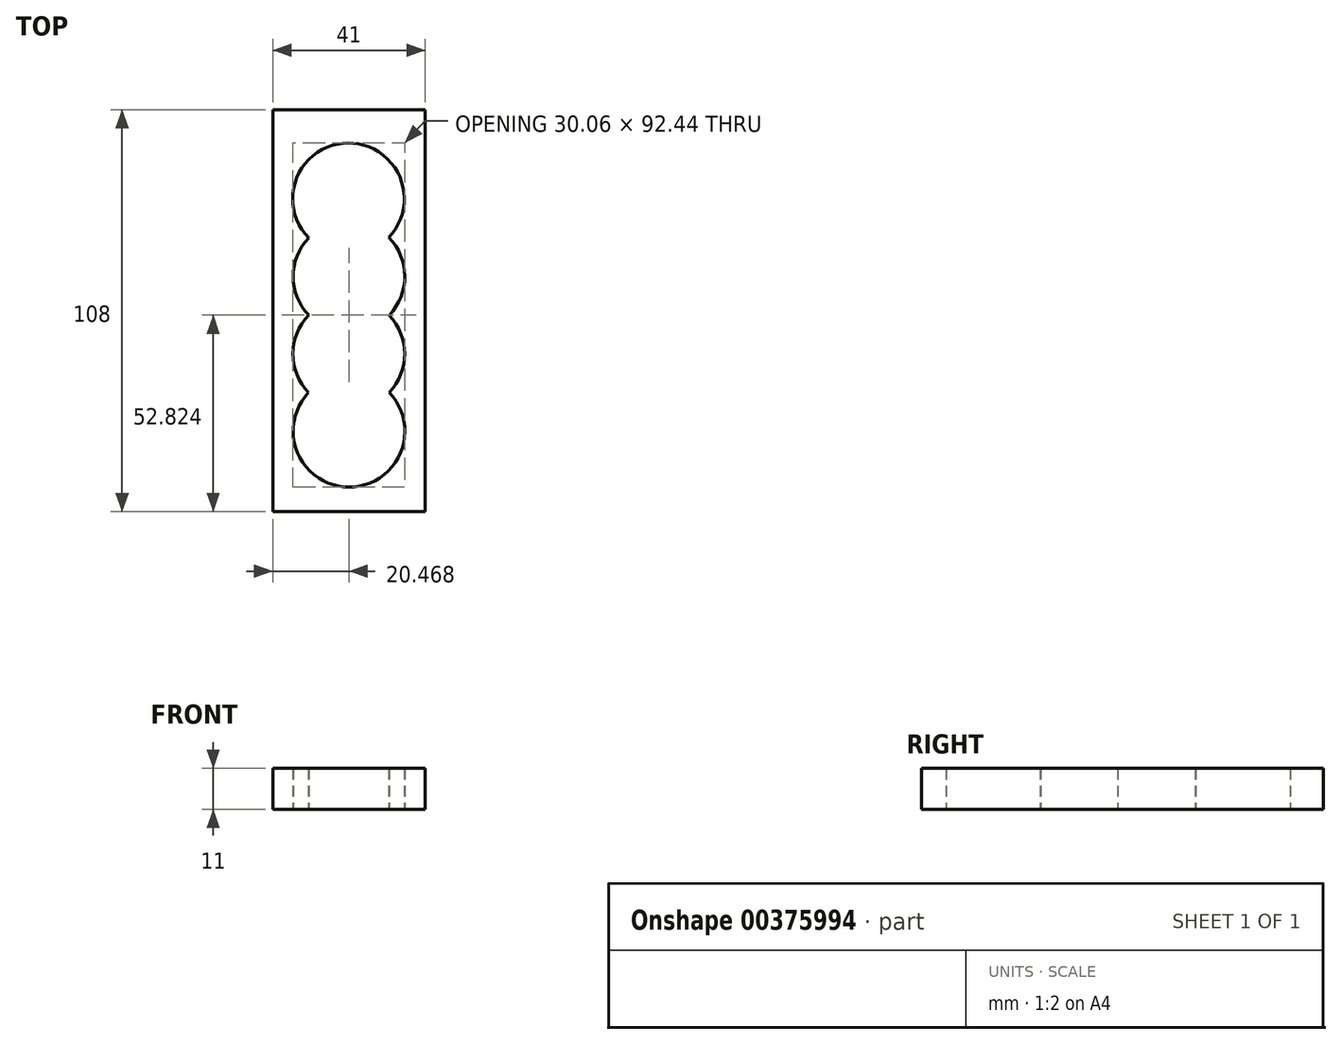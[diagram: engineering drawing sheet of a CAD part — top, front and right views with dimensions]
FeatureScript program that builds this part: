
annotation { "Feature Type Name" : "Feature", "Feature Type Description" : "" }
export const myFeature = defineFeature(function(context is Context, id is Id, definition is map)
    precondition{}
    {
        {
            var Q0;
            Q0=qCreatedBy(makeId("Top.planeOp"),FACE);
            var sketch = newSketch(context, id + "F0", { "sketchPlane" : qUnion([Q0])});
            skLineSegment(sketch, "E0", {"start": v(-0.18, 42.76) * mm, "end": v(0, -38.86) * mm, "construction": true});
            skCircle(sketch, "E1", {"center": v(-0.06, -12.62) * mm, "radius": 9 * mm});
            skCircle(sketch, "E2", {"center": v(-0.1, 8.22) * mm, "radius": 9 * mm});
            skCircle(sketch, "E3", {"center": v(-0.15, 29.04) * mm, "radius": 9 * mm});
            skPoint(sketch, "E4.oppositeSnap0", {"position": v(8.9, -24.62) * mm});
            skPoint(sketch, "E5.endSnap0", {"position": v(-13.1, -24.62) * mm});
            skCircle(sketch, "E6", {"center": v(10.35, 29.04) * mm, "radius": 1.25 * mm});
            skCircle(sketch, "E7", {"center": v(10.35, 8.22) * mm, "radius": 1.25 * mm});
            skCircle(sketch, "E8", {"center": v(10.35, -12.62) * mm, "radius": 1.25 * mm});
            skCircle(sketch, "E9.MirrorC", {"center": v(-10.65, 29) * mm, "radius": 1.25 * mm});
            skCircle(sketch, "E10.MirrorC", {"center": v(-10.56, 8.18) * mm, "radius": 1.25 * mm});
            skCircle(sketch, "E11.MirrorC", {"center": v(-10.47, -12.67) * mm, "radius": 1.25 * mm});
            skCircle(sketch, "E12", {"center": v(10.35, -33.38) * mm, "radius": 1.25 * mm});
            skCircle(sketch, "E13", {"center": v(-10.47, -33.43) * mm, "radius": 1.25 * mm});
            skCircle(sketch, "E14", {"center": v(-0.02, -33.4) * mm, "radius": 9 * mm});
            skLineSegment(sketch, "E15", {"start": v(-0.1, 8.22) * mm, "end": v(-23.14, 8.17) * mm, "construction": true});
            skLineSegment(sketch, "E16", {"start": v(-0.06, -12.62) * mm, "end": v(-20.8, -12.67) * mm, "construction": true});
            skLineSegment(sketch, "E17", {"start": v(12.8, -12.1) * mm, "end": v(12.8, -12.85) * mm});
            skLineSegment(sketch, "E18", {"start": v(-13.03, -12.27) * mm, "end": v(-13.03, -12.78) * mm});
            skLineSegment(sketch, "E19", {"start": v(-13.37, 8.31) * mm, "end": v(-13.37, 8.08) * mm});
            skLineSegment(sketch, "E20", {"start": v(13.19, 8.34) * mm, "end": v(13.19, 8.17) * mm});
            skCircle(sketch, "E21", {"center": v(-10.47, -12.67) * mm, "radius": 2.25 * mm});
            skCircle(sketch, "E22", {"center": v(10.35, -12.62) * mm, "radius": 2.25 * mm});
            skPoint(sketch, "E23.startSnap0", {"position": v(-9, -2.31) * mm});
            skPoint(sketch, "E23.endSnap0", {"position": v(-9.76, -22) * mm});
            skPoint(sketch, "E24.startSnap0", {"position": v(-9.04, 18.63) * mm});
            skCircle(sketch, "E25", {"center": v(-0.15, 29.04) * mm, "radius": 15 * mm});
            skCircle(sketch, "E26", {"center": v(-0.02, -33.4) * mm, "radius": 15 * mm});
            skCircle(sketch, "E27", {"center": v(-10.56, 8.18) * mm, "radius": 2.5 * mm});
            skCircle(sketch, "E28", {"center": v(10.35, 8.22) * mm, "radius": 2.5 * mm});
            skCircle(sketch, "E29", {"center": v(10.35, 29.04) * mm, "radius": 2.5 * mm});
            skCircle(sketch, "E30", {"center": v(-10.65, 29) * mm, "radius": 2.5 * mm});
            skCircle(sketch, "E31", {"center": v(-10.47, -33.43) * mm, "radius": 2.5 * mm});
            skCircle(sketch, "E32", {"center": v(10.35, -33.38) * mm, "radius": 2.5 * mm});
            skCircle(sketch, "E33", {"center": v(-0.06, -12.62) * mm, "radius": 15 * mm});
            skCircle(sketch, "E34", {"center": v(0, 8.16) * mm, "radius": 15 * mm});
            skLineSegment(sketch, "E35.bottom", {"start": v(-20.5, 53) * mm, "end": v(20.5, 53) * mm});
            skLineSegment(sketch, "E35.top", {"start": v(-20.5, -55) * mm, "end": v(20.5, -55) * mm});
            skLineSegment(sketch, "E35.left", {"start": v(-20.5, 53) * mm, "end": v(-20.5, -55) * mm});
            skLineSegment(sketch, "E35.right", {"start": v(20.5, 53) * mm, "end": v(20.5, -55) * mm});
            skSolve(sketch);
        }
        {
            var Q0;
            Q0 = qSketchRegion(id + "F0", true);
            extrude(context, id + "F1", {"entities" : qUnion([Q0]), "depth" : 11 * mm});
        }
    });
